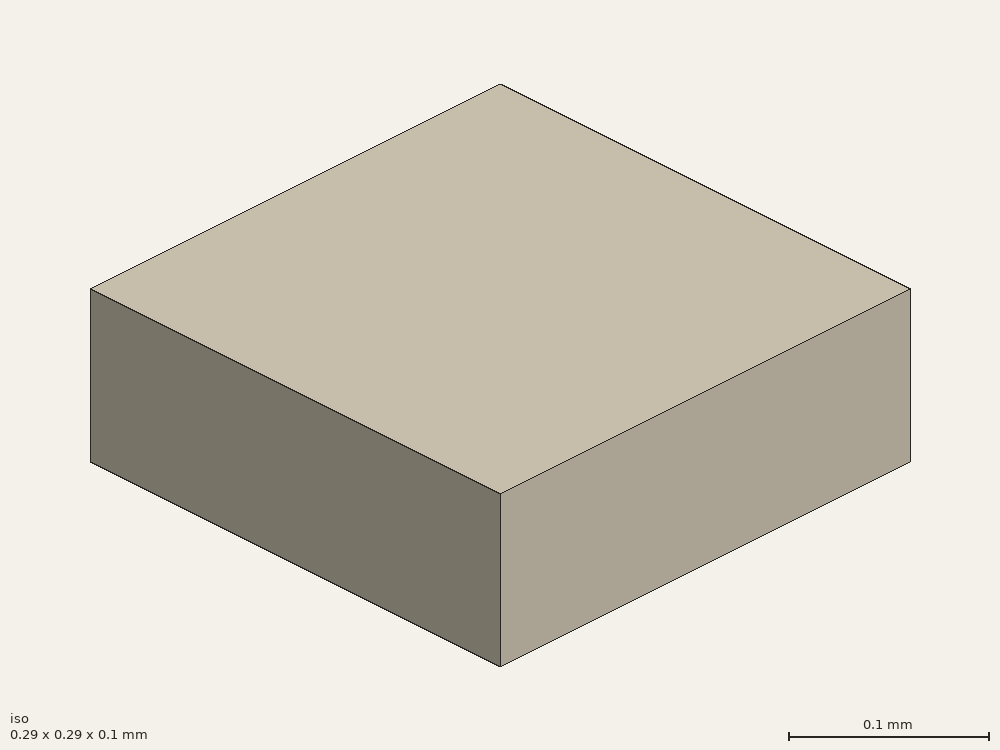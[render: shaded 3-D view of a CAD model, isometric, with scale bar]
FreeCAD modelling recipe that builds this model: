
FCSTD DOCUMENT  (FreeCAD 0.17R12607 (Git))
Label: 1616 RGB LED Green
License: CreativeCommons Attribution-ShareAlike
LicenseURL: http://creativecommons.org/licenses/by-sa/4.0/
objects: Sketcher::SketchObject×1, PartDesign::Pad×1, PartDesign::Body×1
note: 4 computed .brp shape members not serialized (recipe doc carries the construction recipe); baked Part::Feature solids carry a one-line shape summary decoded from their .brp

FEATURE [Sketcher::SketchObject] Sketch
  MapMode = 5
  Support = -> [XY_Plane]
  sketch-geometry (4):
    g0: LineSegment StartX=-0.145 StartY=0.145 StartZ=0 EndX=0.145 EndY=0.145 EndZ=0
    g1: LineSegment StartX=0.145 StartY=0.145 StartZ=0 EndX=0.145 EndY=-0.145 EndZ=0
    g2: LineSegment StartX=0.145 StartY=-0.145 StartZ=0 EndX=-0.145 EndY=-0.145 EndZ=0
    g3: LineSegment StartX=-0.145 StartY=-0.145 StartZ=0 EndX=-0.145 EndY=0.145 EndZ=0
  constraints (12):
    c: Coincident(g0,g1)
    c: Coincident(g1,g2)
    c: Coincident(g2,g3)
    c: Coincident(g3,g0)
    c: Horizontal(g0)
    c: Horizontal(g2)
    c: Vertical(g1)
    c: Vertical(g3)
    c: Symmetric(g0,g0,g-2)
    c: Symmetric(g0,g1,g-1)
    c: Equal(g0,g1)
    c: DistanceY(g1,g1) = 0.29
FEATURE [PartDesign::Pad] Pad
  Length = 0.1
  Length2 = 100
  Profile = -> Sketch
  Type = 0
FEATURE [PartDesign::Body] Body
  Group = -> [Sketch,Pad]
  Origin = -> Origin
  Tip = -> Pad
